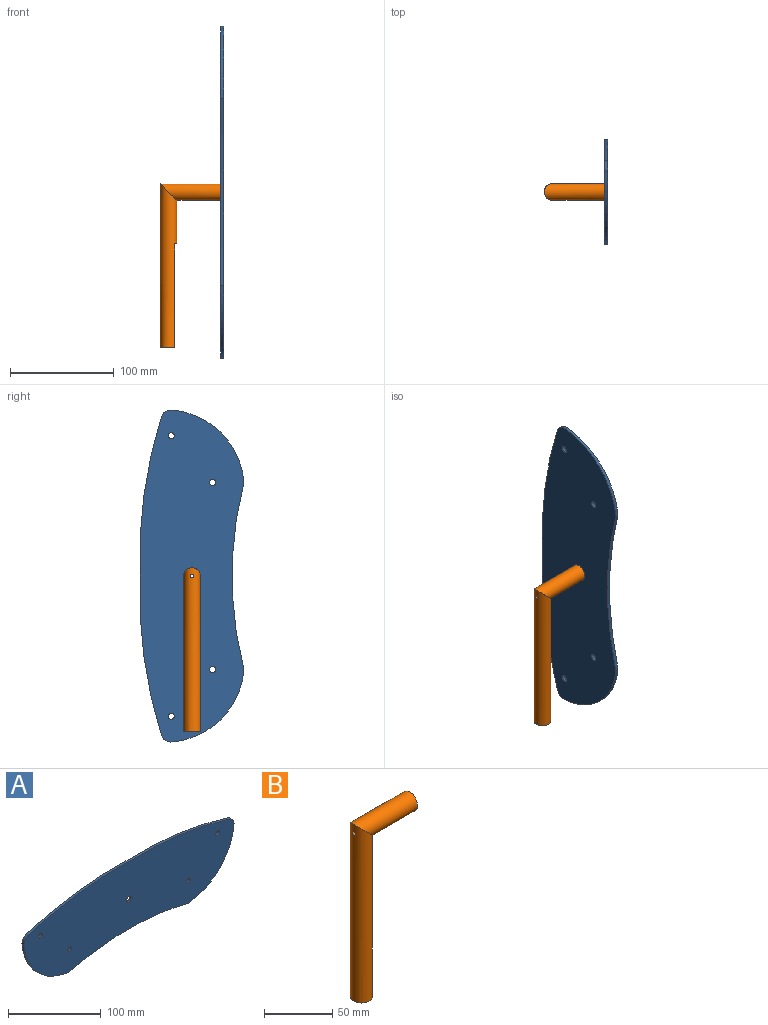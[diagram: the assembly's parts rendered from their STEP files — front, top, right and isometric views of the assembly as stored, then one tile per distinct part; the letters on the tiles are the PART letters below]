
ASSEMBLY  parts=2 mates=1
PART A: 14 faces, bbox 319.5x3x100.3 mm
  f0: cylinder r=453.35mm len=152.76mm, axis (0,1,0), area 464.6mm2, adj f8,f10,f11,f13
  f1: cylinder r=76.01mm len=69.43mm, axis (0,1,0), area 319.5mm2, adj f2,f10,f11,f13
  f2: cylinder r=359.49mm len=180.6mm, axis (0,1,0), area 547.7mm2, adj f1,f3,f10,f11
  f3: cylinder r=76.01mm len=69.43mm, axis (0,1,0), area 319.5mm2, adj f2,f10,f11,f12
  f4: cylinder r=3mm len=6mm, axis (0,1,0), area 56.5mm2, adj f10,f11
  f5: cylinder r=4mm len=8mm, axis (0,1,0), area 75.4mm2, adj f10,f11
  f6: cylinder r=3mm len=6mm, axis (0,1,0), area 56.5mm2, adj f10,f11
  f7: cylinder r=3mm len=6mm, axis (0,1,0), area 56.5mm2, adj f10,f11
  f8: cylinder r=453.35mm len=152.76mm, axis (0,1,0), area 464.6mm2, adj f0,f10,f11,f12
  f9: cylinder r=3mm len=6mm, axis (0,1,0), area 56.5mm2, adj f10,f11
  f10: plane 319.53x100.33mm, normal (0,-1,0), area 25906.2mm2, adj f0,f1,f2,f3,f4,f5,f6,f7
  f11: plane 319.53x100.33mm, normal (0,1,0), area 25906.2mm2, adj f0,f1,f2,f3,f4,f5,f6,f7
  f12: cylinder r=10mm len=10.41mm, axis (0,1,0), area 40.6mm2, adj f3,f8,f10,f11
  f13: cylinder r=10mm len=10.41mm, axis (0,1,0), area 40.6mm2, adj f0,f1,f10,f11
PART B: 7 faces, bbox 58x16x158 mm
  f0: cylinder r=8mm len=158mm, axis (0,0,1), area 6359.2mm2, adj f2,f3,f4,f5,f6
  f1: plane 16x16mm, normal (1,0,0), area 192mm2, adj f3,f6
  f2: plane 16x13.94mm, normal (0,0,-1), area 186mm2, adj f0,f4
  f3: cylinder r=8mm len=58mm, axis (1,0,0), area 2515.2mm2, adj f0,f1
  f4: plane 100x10.71mm, normal (1,0,0), area 1071.1mm2, adj f0,f2,f5
  f5: plane 10.71x2.06mm, normal (0,0,-1), area 15.1mm2, adj f0,f4
  f6: cylinder r=1.7mm len=58mm, axis (1,0,0), area 617.9mm2, adj f0,f1
PLACE A rot(axis=(-0.58,0.58,0.58),120deg) t=(36.67,32.72,113.45)mm
PLACE B t=(-13.33,32.72,-36.55)mm fixed
MATE revolute A.f5 <-> B.f3  axis (-1,0,0) through (36.67,32.72,113.45)mm
